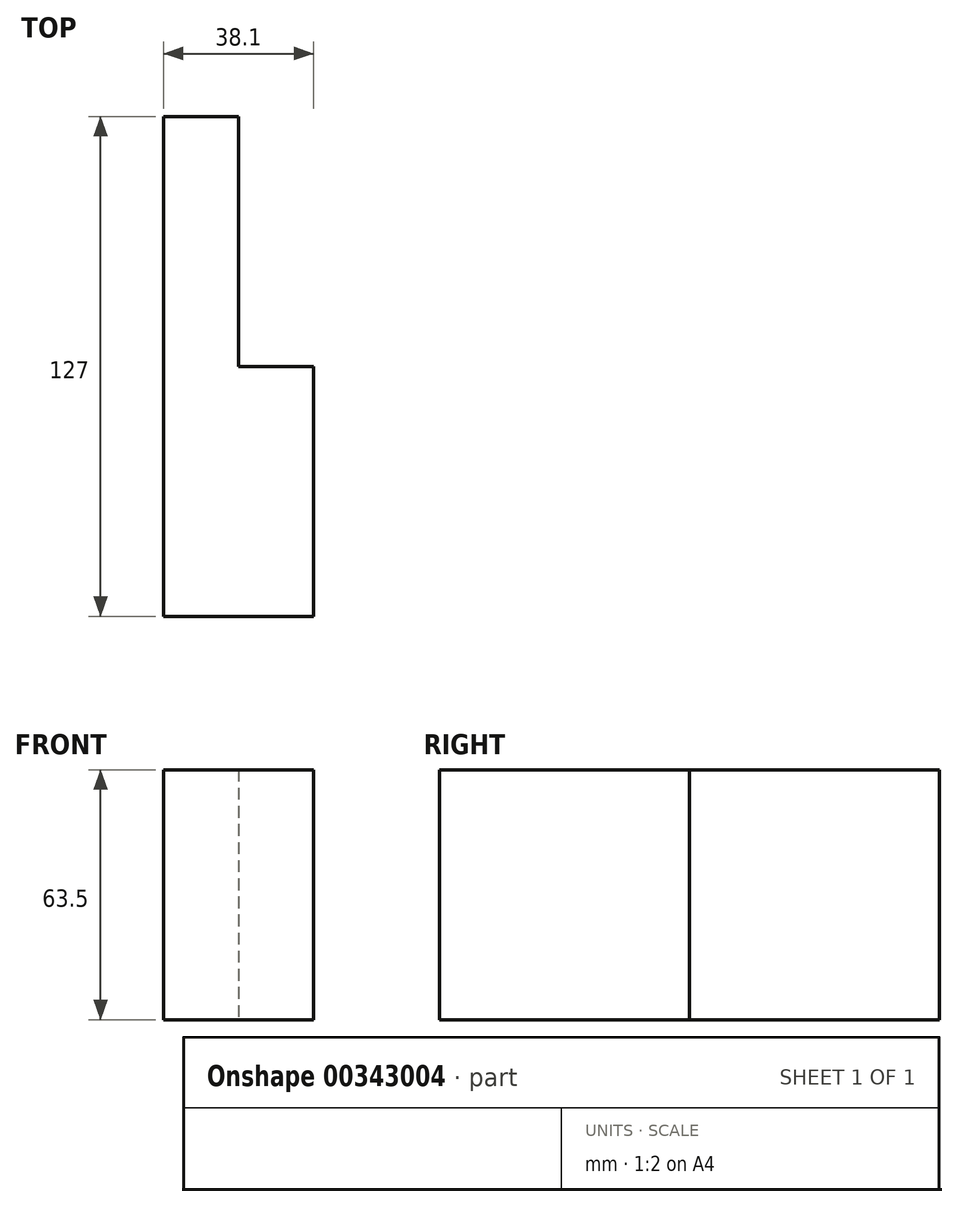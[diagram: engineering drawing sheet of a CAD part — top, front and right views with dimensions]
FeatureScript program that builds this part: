
annotation { "Feature Type Name" : "Feature", "Feature Type Description" : "" }
export const myFeature = defineFeature(function(context is Context, id is Id, definition is map)
    precondition{}
    {
        {
            var Q0;
            Q0=qCreatedBy(makeId("Front.planeOp"),FACE);
            var sketch = newSketch(context, id + "F0", { "sketchPlane" : qUnion([Q0])});
            skLineSegment(sketch, "E0", {"start": v(-6.12, 18.49) * mm, "end": v(-6.12, -45.01) * mm});
            skLineSegment(sketch, "E1", {"start": v(-6.12, 18.49) * mm, "end": v(31.98, 18.49) * mm});
            skLineSegment(sketch, "E2", {"start": v(31.98, 18.49) * mm, "end": v(31.98, -45.01) * mm});
            skLineSegment(sketch, "E3", {"start": v(31.98, -45.01) * mm, "end": v(-6.12, -45.01) * mm});
            skLineSegment(sketch, "E4", {"start": v(12.93, 18.49) * mm, "end": v(12.93, -45.01) * mm});
            skSolve(sketch);
        }
        {
            var Q0;
            Q0 = qSketchRegion(id + "F0", true);
            extrude(context, id + "F1", {"entities" : qUnion([Q0]), "depth" : 127 * mm});
        }
        {
            var Q0;
            {var subQ0=sQuery(id+"F0.wireOp",EDGE,"E2");Q0=makeQuery(id+"F0.imprint","IMPRINT",FACE,{"disambiguationData":[TD([[makeQuery(id+"F0.imprint","IMPRINT",EDGE,{"derivedFrom":subQ0}),-1.0]])]});}
            extrude(context, id + "F2", {"entities" : qUnion([Q0]), "operationType" : NewBodyOperationType.REMOVE, "depth" : 63.5 * mm});
        }
    });
